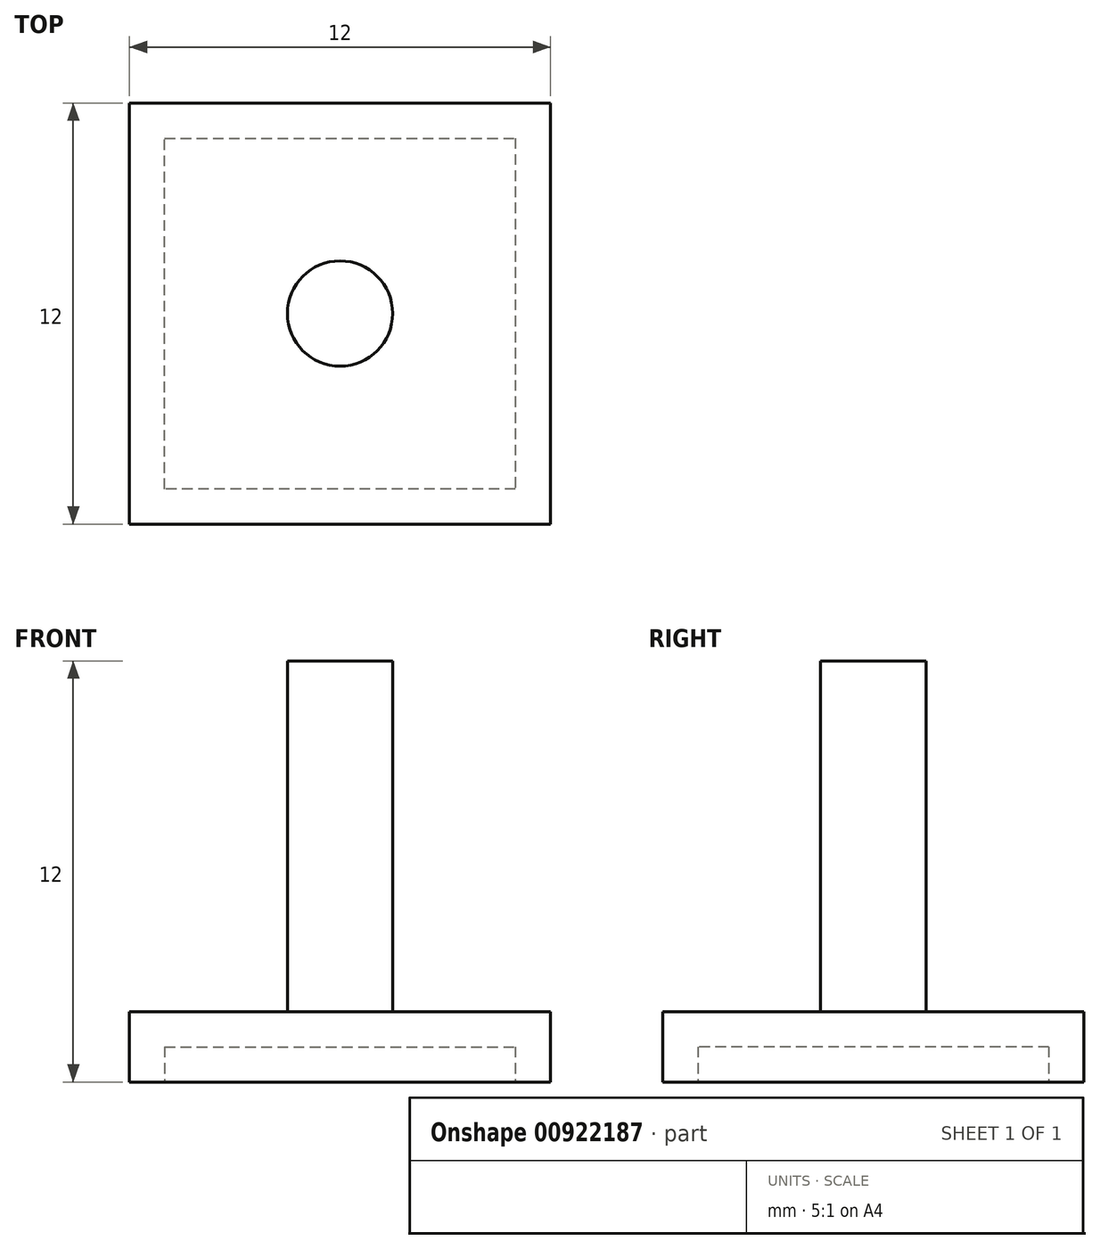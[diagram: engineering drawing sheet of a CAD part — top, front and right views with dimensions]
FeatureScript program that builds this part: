
annotation { "Feature Type Name" : "Feature", "Feature Type Description" : "" }
export const myFeature = defineFeature(function(context is Context, id is Id, definition is map)
    precondition{}
    {
        {
            var Q0;
            Q0=qCreatedBy(makeId("Top.planeOp"),FACE);
            var sketch = newSketch(context, id + "F0", { "sketchPlane" : qUnion([Q0])});
            skLineSegment(sketch, "E0.bottom", {"start": v(6, -6) * mm, "end": v(-6, -6) * mm});
            skLineSegment(sketch, "E0.top", {"start": v(6, 6) * mm, "end": v(-6, 6) * mm});
            skLineSegment(sketch, "E0.left", {"start": v(6, -6) * mm, "end": v(6, 6) * mm});
            skLineSegment(sketch, "E0.right", {"start": v(-6, -6) * mm, "end": v(-6, 6) * mm});
            skPoint(sketch, "E0.middle", {"position": v(0, 0) * mm});
            skSolve(sketch);
        }
        {
            var Q0;
            Q0=makeQuery(id+"F0.imprint","IMPRINT",FACE,{"disambiguationData":[TD([[makeQuery(id+"F0.imprint","IMPRINT",EDGE,{"derivedFrom":sQuery(id+"F0.wireOp",EDGE,"E0.bottom")}),-1.0]])]});
            extrude(context, id + "F1", {"entities" : qUnion([Q0]), "depth" : 2 * mm, "offsetDistance" : 25 * mm});
        }
        {
            var Q0;
            Q0=makeQuery(id+"F1.opExtrude","CAP_FACE",FACE,{"disambiguationData":[OSD([sQuery(id+"F0.wireOp",EDGE,"E0.bottom"),sQuery(id+"F0.wireOp",EDGE,"E0.top"),sQuery(id+"F0.wireOp",EDGE,"E0.left"),sQuery(id+"F0.wireOp",EDGE,"E0.right")])],"isStart":false});
            var sketch = newSketch(context, id + "F2", { "sketchPlane" : qUnion([Q0])});
            skCircle(sketch, "E1", {"center": v(0, 0) * mm, "radius": 1.5 * mm});
            skSolve(sketch);
        }
        {
            var Q0;
            Q0=makeQuery(id+"F2.imprint","IMPRINT",FACE,{"disambiguationData":[TD([[makeQuery(id+"F2.imprint","IMPRINT",EDGE,{"derivedFrom":sQuery(id+"F2.wireOp",EDGE,"E1")}),1.0]])]});
            extrude(context, id + "F3", {"entities" : qUnion([Q0]), "operationType" : NewBodyOperationType.ADD, "depth" : 10 * mm, "offsetDistance" : 25 * mm});
        }
        {
            var Q0;
            Q0=makeQuery(id+"F1.opExtrude","CAP_FACE",FACE,{"disambiguationData":[OSD([sQuery(id+"F0.wireOp",EDGE,"E0.bottom"),sQuery(id+"F0.wireOp",EDGE,"E0.top"),sQuery(id+"F0.wireOp",EDGE,"E0.left"),sQuery(id+"F0.wireOp",EDGE,"E0.right")])],"isStart":true});
            var sketch = newSketch(context, id + "F4", { "sketchPlane" : qUnion([Q0])});
            skLineSegment(sketch, "E2.0", {"start": v(5, -5) * mm, "end": v(5, 5) * mm});
            skLineSegment(sketch, "E2.1", {"start": v(-5, -5) * mm, "end": v(5, -5) * mm});
            skLineSegment(sketch, "E2.2", {"start": v(-5, 5) * mm, "end": v(-5, -5) * mm});
            skLineSegment(sketch, "E2.3", {"start": v(5, 5) * mm, "end": v(-5, 5) * mm});
            skSolve(sketch);
        }
        {
            var Q0;
            Q0=makeQuery(id+"F4.imprint","IMPRINT",FACE,{"disambiguationData":[TD([[makeQuery(id+"F4.imprint","IMPRINT",EDGE,{"derivedFrom":sQuery(id+"F4.wireOp",EDGE,"E2.0")}),1.0]])]});
            extrude(context, id + "F5", {"entities" : qUnion([Q0]), "operationType" : NewBodyOperationType.REMOVE, "oppositeDirection" : true, "depth" : 1 * mm, "offsetDistance" : 25 * mm});
        }
    });
